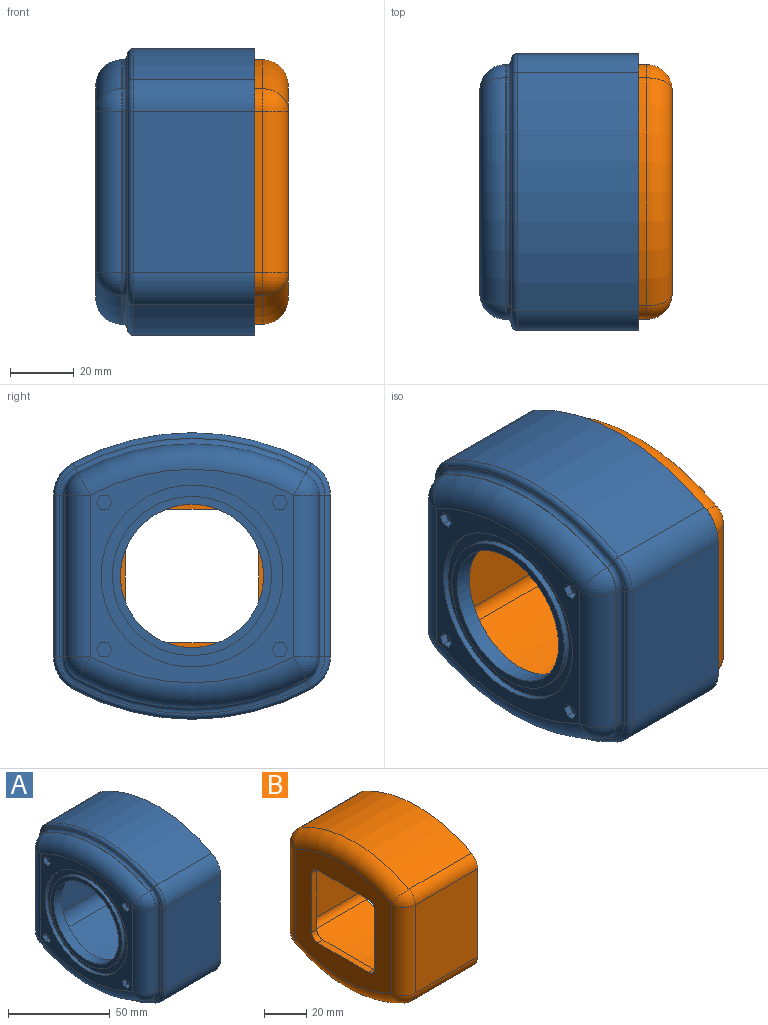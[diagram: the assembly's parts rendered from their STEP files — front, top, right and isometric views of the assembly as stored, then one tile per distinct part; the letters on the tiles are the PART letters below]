
ASSEMBLY  parts=2 mates=1
PART A: 146 faces, bbox 50.1x89x103.1 mm
  f0: plane 90.11x87mm, normal (1,0,0), area 1037.4mm2, adj f6,f7,f8,f9,f22,f23,f24,f25
  f1: plane 67.11x64mm, normal (-1,0,0), area 1323.3mm2, adj f13,f14,f18,f19,f43,f46,f47,f48
  f2: plane 50.84x0.25mm, normal (0,1,0), area 12.7mm2, adj f15,f19,f21,f31
  f3: cylinder r=75mm len=71.64mm, axis (-1,0,0), area 18.7mm2, adj f12,f18,f21,f26
  f4: plane 50.84x0.25mm, normal (0,-1,0), area 12.7mm2, adj f10,f12,f13,f32
  f5: cylinder r=75mm len=71.64mm, axis (-1,0,0), area 18.7mm2, adj f10,f14,f15,f39
  f6: cylinder r=78.5mm len=74.99mm, axis (-1,0,0), area 2990.2mm2, adj f0,f22,f25,f29
  f7: plane 50.84x38.25mm, normal (0,-1,0), area 1944.7mm2, adj f0,f22,f23,f37
  f8: cylinder r=78.5mm len=74.99mm, axis (-1,0,0), area 2990.2mm2, adj f0,f23,f24,f41
  f9: plane 50.84x38.25mm, normal (0,1,0), area 1944.7mm2, adj f0,f24,f25,f34
  f10: cylinder r=8mm len=7.03mm, axis (-1,0,0), area 2.1mm2, adj f4,f5,f11,f36
  f11: sphere r=8mm, area 68.7mm2, adj f10,f13,f14
  f12: cylinder r=8mm len=7.03mm, axis (-1,0,0), area 2.1mm2, adj f3,f4,f16,f28
  f13: cylinder r=8mm len=50.84mm, axis (0,0,-1), area 638.9mm2, adj f1,f4,f11,f16
  f14: torus R=67mm, axis (1,0,0), area 902.2mm2, adj f1,f5,f11,f17
  f15: cylinder r=8mm len=7.03mm, axis (-1,0,0), area 2.1mm2, adj f2,f5,f17,f35
  f16: sphere r=8mm, area 68.7mm2, adj f12,f13,f18
  f17: sphere r=8mm, area 68.7mm2, adj f14,f15,f19
  f18: torus R=67mm, axis (1,0,0), area 902.2mm2, adj f1,f3,f16,f20
  f19: cylinder r=8mm len=50.84mm, axis (0,0,1), area 638.9mm2, adj f1,f2,f17,f20
  f20: sphere r=8mm, area 68.7mm2, adj f18,f19,f21
  f21: cylinder r=8mm len=7.03mm, axis (-1,0,0), area 2.1mm2, adj f2,f3,f20,f27
  f22: cylinder r=11.5mm len=38.25mm, axis (-1,0,0), area 471.9mm2, adj f0,f6,f7,f33
  f23: cylinder r=11.5mm len=38.25mm, axis (-1,0,0), area 471.9mm2, adj f0,f7,f8,f40
  f24: cylinder r=11.5mm len=38.25mm, axis (-1,0,0), area 471.9mm2, adj f0,f8,f9,f38
  f25: cylinder r=11.5mm len=38.25mm, axis (-1,0,0), area 471.9mm2, adj f0,f6,f9,f30
  f26: torus R=76.75mm, axis (1,0,0), area 207.1mm2, adj f3,f27,f28,f29
  f27: torus R=9.75mm, axis (1,0,0), area 25.5mm2, adj f21,f26,f30,f31
  f28: torus R=9.75mm, axis (1,0,0), area 25.5mm2, adj f12,f26,f32,f33
  f29: torus R=76.75mm, axis (1,0,0), area 213.2mm2, adj f6,f26,f30,f33
  f30: torus R=9.75mm, axis (1,0,0), area 32mm2, adj f25,f27,f29,f34
  f31: cylinder r=1.75mm len=50.84mm, axis (0,0,-1), area 139.8mm2, adj f2,f27,f34,f35
  f32: cylinder r=1.75mm len=50.84mm, axis (0,0,1), area 139.8mm2, adj f4,f28,f36,f37
  f33: torus R=9.75mm, axis (1,0,0), area 32mm2, adj f22,f28,f29,f37
  f34: cylinder r=1.75mm len=50.84mm, axis (0,0,1), area 139.8mm2, adj f9,f30,f31,f38
  f35: torus R=9.75mm, axis (1,0,0), area 25.5mm2, adj f15,f31,f38,f39
  f36: torus R=9.75mm, axis (1,0,0), area 25.5mm2, adj f10,f32,f39,f40
  f37: cylinder r=1.75mm len=50.84mm, axis (0,0,-1), area 139.8mm2, adj f7,f32,f33,f40
  f38: torus R=9.75mm, axis (1,0,0), area 32mm2, adj f24,f34,f35,f41
  f39: torus R=76.75mm, axis (1,0,0), area 207.1mm2, adj f5,f35,f36,f41
  f40: torus R=9.75mm, axis (1,0,0), area 32mm2, adj f23,f36,f37,f41
  f41: torus R=76.75mm, axis (1,0,0), area 213.2mm2, adj f8,f38,f39,f40
  f42: cylinder r=25mm len=50mm, axis (-1,0,0), area 290.6mm2, adj f44,f45
  f43: cylinder r=28.6mm len=57.2mm, axis (-1,0,0), area 332.4mm2, adj f1,f44
  f44: plane 57.2x57.2mm, normal (-1,0,0), area 606.2mm2, adj f42,f43
  f45: plane 50x50mm, normal (-1,0,0), area 373.1mm2, adj f42,f145
  f46: plane 2.3x2.15mm, normal (0,0.87,0.5), area 5.7mm2, adj f1,f47,f51,f52
  f47: plane 2.3x2.15mm, normal (0,0.87,-0.5), area 5.7mm2, adj f1,f46,f48,f52
  f48: plane 2.48x2.3mm, normal (0,0,-1), area 5.7mm2, adj f1,f47,f49,f52
  f49: plane 2.3x2.15mm, normal (0,-0.87,-0.5), area 5.7mm2, adj f1,f48,f50,f52
  f50: plane 2.3x2.15mm, normal (0,-0.87,0.5), area 5.7mm2, adj f1,f49,f51,f52
  f51: plane 2.48x2.3mm, normal (0,0,1), area 5.7mm2, adj f1,f46,f50,f52
  f52: plane 4.97x4.3mm, normal (-1,0,0), area 16mm2, adj f46,f47,f48,f49,f50,f51
  f53: plane 2.48x2.3mm, normal (0,0,1), area 5.7mm2, adj f1,f54,f58,f59
  f54: plane 2.3x2.15mm, normal (0,0.87,0.5), area 5.7mm2, adj f1,f53,f55,f59
  f55: plane 2.3x2.15mm, normal (0,0.87,-0.5), area 5.7mm2, adj f1,f54,f56,f59
  f56: plane 2.48x2.3mm, normal (0,0,-1), area 5.7mm2, adj f1,f55,f57,f59
  f57: plane 2.3x2.15mm, normal (0,-0.87,-0.5), area 5.7mm2, adj f1,f56,f58,f59
  f58: plane 2.3x2.15mm, normal (0,-0.87,0.5), area 5.7mm2, adj f1,f53,f57,f59
  f59: plane 4.97x4.3mm, normal (-1,0,0), area 16mm2, adj f53,f54,f55,f56,f57,f58
  f60: plane 2.3x2.15mm, normal (0,-0.87,0.5), area 5.7mm2, adj f1,f61,f65,f66
  f61: plane 2.48x2.3mm, normal (0,0,1), area 5.7mm2, adj f1,f60,f62,f66
  f62: plane 2.3x2.15mm, normal (0,0.87,0.5), area 5.7mm2, adj f1,f61,f63,f66
  f63: plane 2.3x2.15mm, normal (0,0.87,-0.5), area 5.7mm2, adj f1,f62,f64,f66
  f64: plane 2.48x2.3mm, normal (0,0,-1), area 5.7mm2, adj f1,f63,f65,f66
  f65: plane 2.3x2.15mm, normal (0,-0.87,-0.5), area 5.7mm2, adj f1,f60,f64,f66
  f66: plane 4.97x4.3mm, normal (-1,0,0), area 16mm2, adj f60,f61,f62,f63,f64,f65
  f67: plane 2.3x2.15mm, normal (0,0.87,-0.5), area 5.7mm2, adj f1,f68,f72,f73
  f68: plane 2.48x2.3mm, normal (0,0,-1), area 5.7mm2, adj f1,f67,f69,f73
  f69: plane 2.3x2.15mm, normal (0,-0.87,-0.5), area 5.7mm2, adj f1,f68,f70,f73
  f70: plane 2.3x2.15mm, normal (0,-0.87,0.5), area 5.7mm2, adj f1,f69,f71,f73
  f71: plane 2.48x2.3mm, normal (0,0,1), area 5.7mm2, adj f1,f70,f72,f73
  f72: plane 2.3x2.15mm, normal (0,0.87,0.5), area 5.7mm2, adj f1,f67,f71,f73
  f73: plane 4.97x4.3mm, normal (-1,0,0), area 16mm2, adj f67,f68,f69,f70,f71,f72
  f74: plane 64.2x64.2mm, normal (1,0,0), area 1598mm2, adj f83,f84,f85,f86,f87,f88,f119,f120
  f75: sphere r=4.5mm, area 21.4mm2, adj f78,f82,f105,f131
  f76: sphere r=4.5mm, area 21.4mm2, adj f77,f78,f103,f127
  f77: cylinder r=4.5mm len=50.84mm, axis (0,0,-1), area 344.5mm2, adj f76,f79,f87,f89,f92,f97,f127,f128
  f78: torus R=67mm, axis (1,0,0), area 470.1mm2, adj f75,f76,f93,f98,f126,f127,f131,f132
  f79: sphere r=4.5mm, area 21.4mm2, adj f77,f81,f104,f138
  f80: sphere r=4.5mm, area 21.4mm2, adj f81,f82,f106,f123
  f81: torus R=67mm, axis (1,0,0), area 470.1mm2, adj f79,f80,f94,f96,f122,f123,f138,f139
  f82: cylinder r=4.5mm len=50.84mm, axis (0,0,1), area 344.5mm2, adj f75,f80,f90,f91,f95,f119,f123,f124
  f83: plane 5.65x3.26mm, normal (0,0.87,0.5), area 2.9mm2, adj f74,f85,f129,f130
  f84: plane 6.52x2.3mm, normal (0,0,-1), area 10.2mm2, adj f74,f91,f119,f120,f124,f125
  f85: plane 6.52x2.3mm, normal (0,0,1), area 10.2mm2, adj f74,f83,f87,f89,f128,f130
  f86: cylinder r=32.1mm len=42.94mm, axis (-1,0,0), area 87mm2, adj f74,f94,f121,f140
  f87: cylinder r=32.1mm len=34.98mm, axis (-1,0,0), area 68.4mm2, adj f74,f77,f85,f89,f92,f142
  f88: cylinder r=32.1mm len=42.94mm, axis (-1,0,0), area 87mm2, adj f74,f93,f129,f133
  f89: plane 16.97x5.08mm, normal (1,0,0), area 28.8mm2, adj f77,f85,f87,f128
  f90: plane 16.97x5.08mm, normal (1,0,0), area 28.8mm2, adj f82,f119,f135,f136
  f91: plane 16.97x5.08mm, normal (1,0,0), area 28.8mm2, adj f82,f84,f119,f124
  f92: plane 16.97x5.08mm, normal (1,0,0), area 28.8mm2, adj f77,f87,f142,f143
  f93: plane 49.64x9.69mm, normal (1,0,0), area 141.9mm2, adj f78,f88,f126,f129,f132,f133
  f94: plane 49.64x9.69mm, normal (1,0,0), area 141.9mm2, adj f81,f86,f121,f122,f139,f140
  f95: plane 50.84x0.25mm, normal (0,-1,0), area 12.7mm2, adj f82,f105,f106,f114
  f96: cylinder r=71.5mm len=68.3mm, axis (-1,0,0), area 17.8mm2, adj f81,f104,f106,f111
  f97: plane 50.84x0.25mm, normal (0,1,0), area 12.7mm2, adj f77,f103,f104,f115
  f98: cylinder r=71.5mm len=68.3mm, axis (-1,0,0), area 17.8mm2, adj f78,f103,f105,f118
  f99: cylinder r=75mm len=71.64mm, axis (-1,0,0), area 2748.6mm2, adj f0,f107,f110,f111
  f100: plane 50.84x36.8mm, normal (0,1,0), area 1871mm2, adj f0,f107,f108,f115
  f101: cylinder r=75mm len=71.64mm, axis (-1,0,0), area 2748.6mm2, adj f0,f108,f109,f118
  f102: plane 50.84x36.8mm, normal (0,-1,0), area 1871mm2, adj f0,f109,f110,f114
  f103: cylinder r=4.5mm len=3.95mm, axis (-1,0,0), area 1.2mm2, adj f76,f97,f98,f117
  f104: cylinder r=4.5mm len=3.95mm, axis (-1,0,0), area 1.2mm2, adj f79,f96,f97,f113
  f105: cylinder r=4.5mm len=3.95mm, axis (-1,0,0), area 1.2mm2, adj f75,f95,f98,f116
  f106: cylinder r=4.5mm len=3.95mm, axis (-1,0,0), area 1.2mm2, adj f80,f95,f96,f112
  f107: cylinder r=8mm len=36.8mm, axis (-1,0,0), area 315.9mm2, adj f0,f99,f100,f113
  f108: cylinder r=8mm len=36.8mm, axis (-1,0,0), area 315.9mm2, adj f0,f100,f101,f117
  f109: cylinder r=8mm len=36.8mm, axis (-1,0,0), area 315.9mm2, adj f0,f101,f102,f116
  f110: cylinder r=8mm len=36.8mm, axis (-1,0,0), area 315.9mm2, adj f0,f99,f102,f112
  f111: torus R=76.75mm, axis (1,0,0), area 468.1mm2, adj f96,f99,f112,f113
  f112: torus R=9.75mm, axis (1,0,0), area 39.7mm2, adj f106,f110,f111,f114
  f113: torus R=9.75mm, axis (1,0,0), area 39.7mm2, adj f104,f107,f111,f115
  f114: cylinder r=5.25mm len=50.84mm, axis (0,0,-1), area 328.6mm2, adj f95,f102,f112,f116
  f115: cylinder r=5.25mm len=50.84mm, axis (0,0,1), area 328.6mm2, adj f97,f100,f113,f117
  f116: torus R=9.75mm, axis (1,0,0), area 39.7mm2, adj f105,f109,f114,f118
  f117: torus R=9.75mm, axis (1,0,0), area 39.7mm2, adj f103,f108,f115,f118
  f118: torus R=76.75mm, axis (1,0,0), area 468.1mm2, adj f98,f101,f116,f117
  f119: cylinder r=32.1mm len=34.98mm, axis (-1,0,0), area 68.4mm2, adj f74,f82,f84,f90,f91,f135
  f120: plane 5.65x3.26mm, normal (0,-0.87,-0.5), area 2.9mm2, adj f74,f84,f121,f125
  f121: plane 5.65x3.26mm, normal (0,-0.87,0.5), area 13.5mm2, adj f74,f86,f94,f120,f122,f125
  f122: plane 6.53x2.3mm, normal (0,0,1), area 13.7mm2, adj f81,f94,f121,f123,f125
  f123: plane 5.71x3.32mm, normal (0,0.87,0.5), area 13.3mm2, adj f80,f81,f82,f122,f124,f125
  f124: plane 5.65x3.26mm, normal (0,0.87,-0.5), area 14.3mm2, adj f82,f84,f91,f123,f125
  f125: plane 13.05x11.3mm, normal (1,0,0), area 110.6mm2, adj f84,f120,f121,f122,f123,f124
  f126: plane 6.53x2.3mm, normal (0,0,-1), area 13.7mm2, adj f78,f93,f127,f129,f130
  f127: plane 5.71x3.32mm, normal (0,-0.87,-0.5), area 13.3mm2, adj f76,f77,f78,f126,f128,f130
  f128: plane 5.65x3.26mm, normal (0,-0.87,0.5), area 14.3mm2, adj f77,f85,f89,f127,f130
  f129: plane 5.65x3.26mm, normal (0,0.87,-0.5), area 13.5mm2, adj f74,f83,f88,f93,f126,f130
  f130: plane 13.05x11.3mm, normal (1,0,0), area 110.6mm2, adj f83,f85,f126,f127,f128,f129
  f131: plane 5.71x3.32mm, normal (0,0.87,-0.5), area 13.3mm2, adj f75,f78,f82,f132,f136,f137
  f132: plane 6.53x2.3mm, normal (0,0,-1), area 13.7mm2, adj f78,f93,f131,f133,f137
  f133: plane 5.65x3.26mm, normal (0,-0.87,-0.5), area 13.5mm2, adj f74,f88,f93,f132,f134,f137
  f134: plane 5.65x3.26mm, normal (0,-0.87,0.5), area 2.9mm2, adj f74,f133,f135,f137
  f135: plane 6.52x2.3mm, normal (0,0,1), area 10.2mm2, adj f74,f90,f119,f134,f136,f137
  f136: plane 5.65x3.26mm, normal (0,0.87,0.5), area 14.3mm2, adj f82,f90,f131,f135,f137
  f137: plane 13.05x11.3mm, normal (1,0,0), area 110.6mm2, adj f131,f132,f133,f134,f135,f136
  f138: plane 5.71x3.32mm, normal (0,-0.87,0.5), area 13.3mm2, adj f77,f79,f81,f139,f143,f144
  f139: plane 6.53x2.3mm, normal (0,0,1), area 13.7mm2, adj f81,f94,f138,f140,f144
  f140: plane 5.65x3.26mm, normal (0,0.87,0.5), area 13.5mm2, adj f74,f86,f94,f139,f141,f144
  f141: plane 5.65x3.26mm, normal (0,0.87,-0.5), area 2.9mm2, adj f74,f140,f142,f144
  f142: plane 6.52x2.3mm, normal (0,0,-1), area 10.2mm2, adj f74,f87,f92,f141,f143,f144
  f143: plane 5.65x3.26mm, normal (0,-0.87,-0.5), area 14.3mm2, adj f77,f92,f138,f142,f144
  f144: plane 13.05x11.3mm, normal (1,0,0), area 110.6mm2, adj f138,f139,f140,f141,f142,f143
  f145: cylinder r=22.5mm len=45mm, axis (-1,0,0), area 756.3mm2, adj f45,f74
PART B: 43 faces, bbox 49.8x80x95.5 mm
  f0: plane 50.84x41.75mm, normal (0,1,0), area 2122.7mm2, adj f4,f11,f15,f17
  f1: cylinder r=75mm len=71.64mm, axis (-1,0,0), area 3118.3mm2, adj f4,f8,f14,f17
  f2: plane 50.84x41.75mm, normal (0,-1,0), area 2122.7mm2, adj f4,f6,f8,f9
  f3: cylinder r=75mm len=71.64mm, axis (-1,0,0), area 3118.3mm2, adj f4,f6,f10,f11
  f4: plane 83.11x80mm, normal (1,0,0), area 960.4mm2, adj f0,f1,f2,f3,f6,f8,f11,f17
  f5: plane 67.11x64mm, normal (-1,0,0), area 2206.8mm2, adj f9,f10,f14,f15,f35,f36,f37,f38
  f6: cylinder r=8mm len=41.75mm, axis (-1,0,0), area 358.3mm2, adj f2,f3,f4,f7
  f7: sphere r=8mm, area 68.7mm2, adj f6,f9,f10
  f8: cylinder r=8mm len=41.75mm, axis (-1,0,0), area 358.3mm2, adj f1,f2,f4,f12
  f9: cylinder r=8mm len=50.84mm, axis (0,0,-1), area 638.9mm2, adj f2,f5,f7,f12
  f10: torus R=67mm, axis (1,0,0), area 902.2mm2, adj f3,f5,f7,f13
  f11: cylinder r=8mm len=41.75mm, axis (-1,0,0), area 358.3mm2, adj f0,f3,f4,f13
  f12: sphere r=8mm, area 68.7mm2, adj f8,f9,f14
  f13: sphere r=8mm, area 68.7mm2, adj f10,f11,f15
  f14: torus R=67mm, axis (1,0,0), area 902.2mm2, adj f1,f5,f12,f16
  f15: cylinder r=8mm len=50.84mm, axis (0,0,1), area 638.9mm2, adj f0,f5,f13,f16
  f16: sphere r=8mm, area 68.7mm2, adj f14,f15,f17
  f17: cylinder r=8mm len=41.75mm, axis (-1,0,0), area 358.3mm2, adj f0,f1,f4,f16
  f18: plane 50.84x41.75mm, normal (0,-1,0), area 2122.7mm2, adj f4,f28,f32,f34
  f19: cylinder r=71.5mm len=68.3mm, axis (-1,0,0), area 2972.8mm2, adj f4,f25,f31,f34
  f20: plane 50.84x41.75mm, normal (0,1,0), area 2122.7mm2, adj f4,f23,f25,f26
  f21: cylinder r=71.5mm len=68.3mm, axis (-1,0,0), area 2972.8mm2, adj f4,f23,f27,f28
  f22: plane 67.11x64mm, normal (1,0,0), area 2206.8mm2, adj f26,f27,f31,f32,f35,f36,f37,f38
  f23: cylinder r=4.5mm len=41.75mm, axis (-1,0,0), area 201.6mm2, adj f4,f20,f21,f24
  f24: sphere r=4.5mm, area 21.7mm2, adj f23,f26,f27
  f25: cylinder r=4.5mm len=41.75mm, axis (-1,0,0), area 201.6mm2, adj f4,f19,f20,f29
  f26: cylinder r=4.5mm len=50.84mm, axis (0,0,-1), area 359.4mm2, adj f20,f22,f24,f29
  f27: torus R=67mm, axis (1,0,0), area 491.8mm2, adj f21,f22,f24,f30
  f28: cylinder r=4.5mm len=41.75mm, axis (-1,0,0), area 201.6mm2, adj f4,f18,f21,f30
  f29: sphere r=4.5mm, area 21.7mm2, adj f25,f26,f31
  f30: sphere r=4.5mm, area 21.7mm2, adj f27,f28,f32
  f31: torus R=67mm, axis (1,0,0), area 491.8mm2, adj f19,f22,f29,f33
  f32: cylinder r=4.5mm len=50.84mm, axis (0,0,1), area 359.4mm2, adj f18,f22,f30,f33
  f33: sphere r=4.5mm, area 21.7mm2, adj f31,f32,f34
  f34: cylinder r=4.5mm len=41.75mm, axis (-1,0,0), area 201.6mm2, adj f4,f18,f19,f33
  f35: cylinder r=4mm len=4mm, axis (-1,0,0), area 22mm2, adj f5,f22,f36,f40
  f36: plane 34x3.5mm, normal (0,0,-1), area 119mm2, adj f5,f22,f35,f37
  f37: cylinder r=4mm len=4mm, axis (-1,0,0), area 22mm2, adj f5,f22,f36,f38
  f38: plane 34x3.5mm, normal (0,-1,0), area 119mm2, adj f5,f22,f37,f39
  f39: cylinder r=4mm len=4mm, axis (-1,0,0), area 22mm2, adj f5,f22,f38,f41
  f40: plane 34x3.5mm, normal (0,1,0), area 119mm2, adj f5,f22,f35,f42
  f41: plane 34x3.5mm, normal (0,0,1), area 119mm2, adj f5,f22,f39,f42
  f42: cylinder r=4mm len=4mm, axis (-1,0,0), area 22mm2, adj f5,f22,f40,f41
PLACE A at identity fixed
PLACE B rot(axis=(0,0,1),180deg) t=(55.47,0,0)mm
MATE fastened B.f0 <-> A.f100  axis (0,-1,0) through (26.6,-40,0)mm
